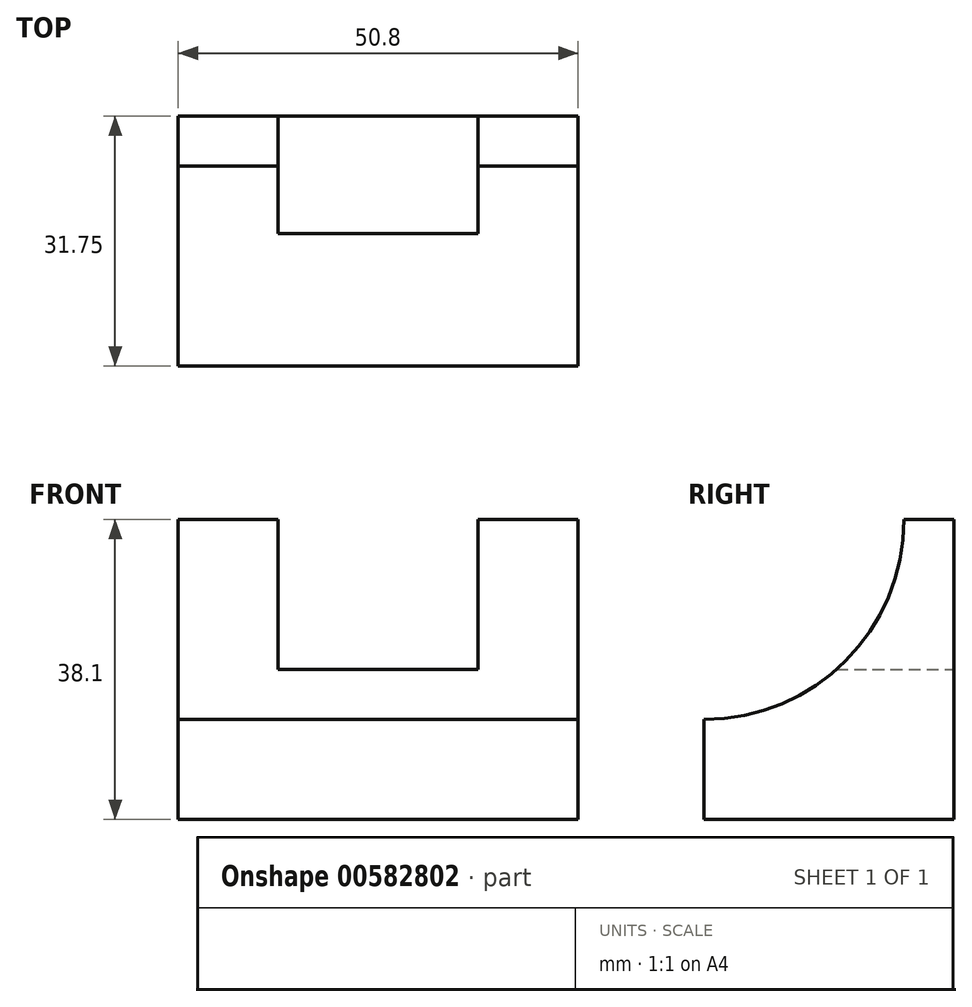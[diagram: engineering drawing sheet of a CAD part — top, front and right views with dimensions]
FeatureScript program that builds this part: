
annotation { "Feature Type Name" : "Feature", "Feature Type Description" : "" }
export const myFeature = defineFeature(function(context is Context, id is Id, definition is map)
    precondition{}
    {
        {
            var Q0;
            Q0=qCreatedBy(makeId("Right.planeOp"),FACE);
            var sketch = newSketch(context, id + "F0", { "sketchPlane" : qUnion([Q0])});
            skLineSegment(sketch, "E0", {"start": v(-25.4, 21.74) * mm, "end": v(-25.4, 9.04) * mm});
            skLineSegment(sketch, "E1", {"start": v(-25.4, 9.04) * mm, "end": v(6.35, 9.04) * mm});
            skLineSegment(sketch, "E2", {"start": v(6.35, 9.04) * mm, "end": v(6.35, 47.14) * mm});
            skLineSegment(sketch, "E3", {"start": v(6.35, 47.14) * mm, "end": v(0, 47.14) * mm});
            skLineSegment(sketch, "E4", {"start": v(0, 47.14) * mm, "end": v(0, 21.74) * mm});
            skLineSegment(sketch, "E5", {"start": v(0, 21.74) * mm, "end": v(-25.4, 21.74) * mm});
            skPoint(sketch, "E6", {"position": v(0, 34.44) * mm});
            skArc(sketch, "E7", {"start": v(-25.4, 21.74) * mm, "mid": v(-7.44, 29.18) * mm, "end": v(0, 47.14) * mm});
            skSolve(sketch);
        }
        {
            var Q0;
            Q0 = qSketchRegion(id + "F0", true);
            extrude(context, id + "F1", {"entities" : qUnion([Q0]), "depth" : 50.8 * mm, "offsetDistance" : 25.4 * mm});
        }
        {
            var Q0;
            Q0=makeQuery(id+"F1.opExtrude","SWEPT_FACE",FACE,{"disambiguationData":[OSD([sQuery(id+"F0.wireOp",EDGE,"E2")])]});
            var sketch = newSketch(context, id + "F2", { "sketchPlane" : qUnion([Q0])});
            skLineSegment(sketch, "E8", {"start": v(-38.1, 47.14) * mm, "end": v(-38.1, 28.1) * mm});
            skLineSegment(sketch, "E9", {"start": v(-38.1, 28.1) * mm, "end": v(-12.7, 28.1) * mm});
            skLineSegment(sketch, "E10", {"start": v(-12.7, 28.1) * mm, "end": v(-12.7, 47.14) * mm});
            skSolve(sketch);
        }
        {
            var Q0;
            {var subQ0=sQuery(id+"F2.wireOp",EDGE,"E8");Q0=makeQuery(id+"F2.imprint","IMPRINT",FACE,{"disambiguationData":[TD([[makeQuery(id+"F2.imprint","IMPRINT",EDGE,{"derivedFrom":subQ0}),1.0]])]});}
            extrude(context, id + "F3", {"entities" : qUnion([Q0]), "operationType" : NewBodyOperationType.REMOVE, "oppositeDirection" : true, "depth" : 15.24 * mm, "offsetDistance" : 25.4 * mm});
        }
    });
